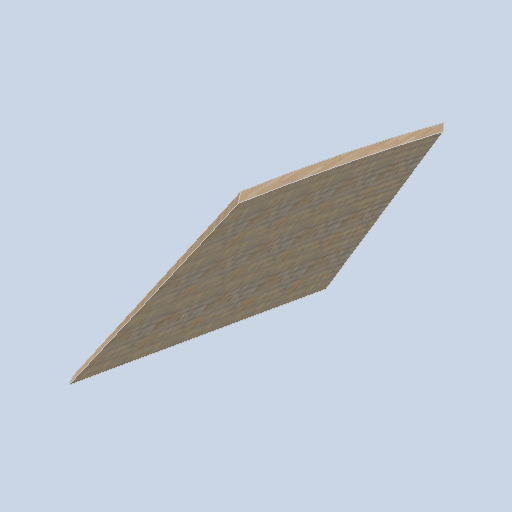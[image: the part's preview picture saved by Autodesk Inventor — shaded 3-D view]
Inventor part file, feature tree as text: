
AUTODESK INVENTOR PART (.ipt)
format: ipt  version: 2024.2 (Build 282272000, 272)  size: 337,408 bytes
history: native  units: mm
features: sketch x3, plane x2, loft x1
ambient origin geometry x8: Origin, YZ Plane, XZ Plane, XY Plane, X Axis, Y Axis, Z Axis, Center Point
bodies: Body1 (feature_tree)
feature tree (6):
  sketch  "Sketch6"  dims[d10=0.0mm d11=1791.0mm d13=0.0mm d14=90.0deg]
  plane  "Work Plane4"
  loft  "Loft3"
  plane  "Work Plane3"
  sketch  "Sketch7"  dims[d15=0.0mm d16=90.0deg]
  sketch  "Sketch8"  dims[d17=50000.0mm]
